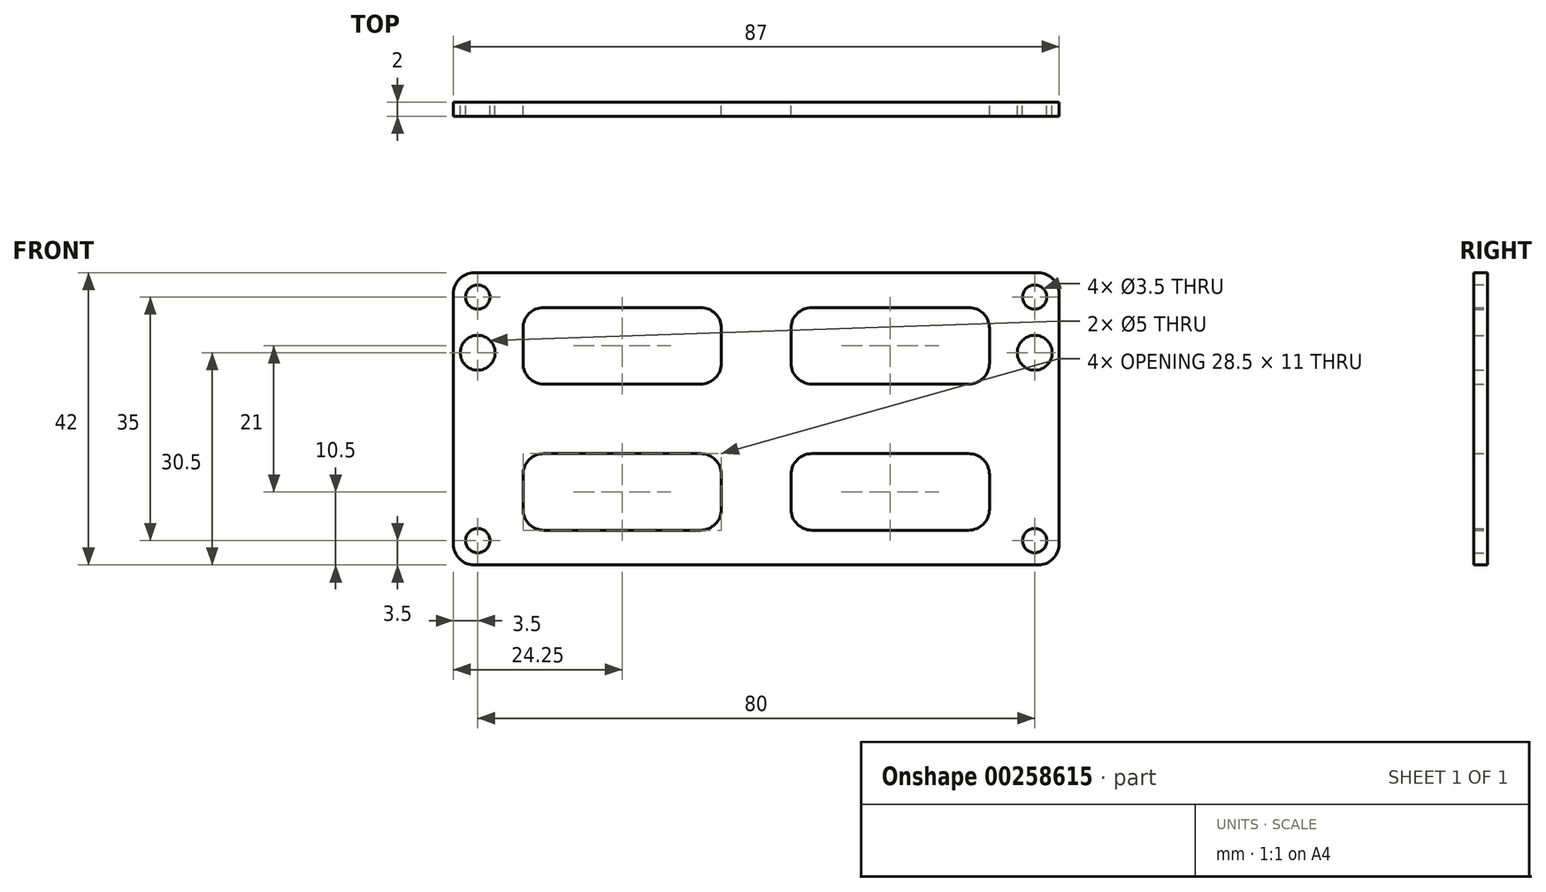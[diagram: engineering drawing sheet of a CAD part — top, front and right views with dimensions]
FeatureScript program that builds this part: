
annotation { "Feature Type Name" : "Feature", "Feature Type Description" : "" }
export const myFeature = defineFeature(function(context is Context, id is Id, definition is map)
    precondition{}
    {
        {
            var Q0;
            Q0=qCreatedBy(makeId("Front.planeOp"),FACE);
            var sketch = newSketch(context, id + "F0", { "sketchPlane" : qUnion([Q0])});
            skLineSegment(sketch, "E0.bottom", {"start": v(40, 17.5) * mm, "end": v(-40, 17.5) * mm, "construction": true});
            skLineSegment(sketch, "E0.top", {"start": v(40, -17.5) * mm, "end": v(-40, -17.5) * mm, "construction": true});
            skLineSegment(sketch, "E0.left", {"start": v(40, 17.5) * mm, "end": v(40, -17.5) * mm, "construction": true});
            skLineSegment(sketch, "E0.right", {"start": v(-40, 17.5) * mm, "end": v(-40, -17.5) * mm, "construction": true});
            skPoint(sketch, "E0.middle", {"position": v(0, 0) * mm});
            skCircle(sketch, "E1", {"center": v(-40, 17.5) * mm, "radius": 1.75 * mm});
            skCircle(sketch, "E2", {"center": v(-40, -17.5) * mm, "radius": 1.75 * mm});
            skCircle(sketch, "E3", {"center": v(40, -17.5) * mm, "radius": 1.75 * mm});
            skCircle(sketch, "E4", {"center": v(40, 17.5) * mm, "radius": 1.75 * mm});
            skLineSegment(sketch, "E5.bottom", {"start": v(-40, 17.5) * mm, "end": v(40, 17.5) * mm, "construction": true});
            skLineSegment(sketch, "E5.top", {"start": v(-40, 9.5) * mm, "end": v(40, 9.5) * mm, "construction": true});
            skLineSegment(sketch, "E5.left", {"start": v(-40, 17.5) * mm, "end": v(-40, 9.5) * mm, "construction": true});
            skLineSegment(sketch, "E5.right", {"start": v(40, 17.5) * mm, "end": v(40, 9.5) * mm, "construction": true});
            skCircle(sketch, "E6", {"center": v(-40, 9.5) * mm, "radius": 2.5 * mm});
            skCircle(sketch, "E7", {"center": v(40, 9.5) * mm, "radius": 2.5 * mm});
            skLineSegment(sketch, "E8.bottom", {"start": v(43.5, 21) * mm, "end": v(-43.5, 21) * mm});
            skLineSegment(sketch, "E8.top", {"start": v(43.5, -21) * mm, "end": v(-43.5, -21) * mm});
            skLineSegment(sketch, "E8.left", {"start": v(43.5, 21) * mm, "end": v(43.5, -21) * mm});
            skLineSegment(sketch, "E8.right", {"start": v(-43.5, 21) * mm, "end": v(-43.5, -21) * mm});
            skLineSegment(sketch, "E9.bottom", {"start": v(5, 5) * mm, "end": v(-5, 5) * mm, "construction": true});
            skLineSegment(sketch, "E9.top", {"start": v(5, -5) * mm, "end": v(-5, -5) * mm, "construction": true});
            skLineSegment(sketch, "E9.left", {"start": v(5, 5) * mm, "end": v(5, -5) * mm, "construction": true});
            skLineSegment(sketch, "E9.right", {"start": v(-5, 5) * mm, "end": v(-5, -5) * mm, "construction": true});
            skLineSegment(sketch, "E10.bottom", {"start": v(-43.5, -21) * mm, "end": v(-33.5, -21) * mm, "construction": true});
            skLineSegment(sketch, "E10.top", {"start": v(-43.5, -16) * mm, "end": v(-33.5, -16) * mm, "construction": true});
            skLineSegment(sketch, "E10.left", {"start": v(-43.5, -21) * mm, "end": v(-43.5, -16) * mm, "construction": true});
            skLineSegment(sketch, "E10.right", {"start": v(-33.5, -21) * mm, "end": v(-33.5, -16) * mm, "construction": true});
            skLineSegment(sketch, "E11.bottom", {"start": v(-43.5, 21) * mm, "end": v(-33.5, 21) * mm, "construction": true});
            skLineSegment(sketch, "E11.top", {"start": v(-43.5, 16) * mm, "end": v(-33.5, 16) * mm, "construction": true});
            skLineSegment(sketch, "E11.left", {"start": v(-43.5, 21) * mm, "end": v(-43.5, 16) * mm, "construction": true});
            skLineSegment(sketch, "E11.right", {"start": v(-33.5, 21) * mm, "end": v(-33.5, 16) * mm, "construction": true});
            skLineSegment(sketch, "E12.bottom", {"start": v(43.5, 21) * mm, "end": v(33.5, 21) * mm, "construction": true});
            skLineSegment(sketch, "E12.top", {"start": v(43.5, 16) * mm, "end": v(33.5, 16) * mm, "construction": true});
            skLineSegment(sketch, "E12.left", {"start": v(43.5, 21) * mm, "end": v(43.5, 16) * mm, "construction": true});
            skLineSegment(sketch, "E12.right", {"start": v(33.5, 21) * mm, "end": v(33.5, 16) * mm, "construction": true});
            skLineSegment(sketch, "E13.bottom", {"start": v(43.5, -21) * mm, "end": v(33.5, -21) * mm, "construction": true});
            skLineSegment(sketch, "E13.top", {"start": v(43.5, -16) * mm, "end": v(33.5, -16) * mm, "construction": true});
            skLineSegment(sketch, "E13.left", {"start": v(43.5, -21) * mm, "end": v(43.5, -16) * mm, "construction": true});
            skLineSegment(sketch, "E13.right", {"start": v(33.5, -21) * mm, "end": v(33.5, -16) * mm, "construction": true});
            skLineSegment(sketch, "E14.bottom", {"start": v(-5, 5) * mm, "end": v(-33.5, 5) * mm});
            skLineSegment(sketch, "E14.top", {"start": v(-5, 16) * mm, "end": v(-33.5, 16) * mm});
            skLineSegment(sketch, "E14.left", {"start": v(-5, 5) * mm, "end": v(-5, 16) * mm});
            skLineSegment(sketch, "E14.right", {"start": v(-33.5, 5) * mm, "end": v(-33.5, 16) * mm});
            skLineSegment(sketch, "E15.bottom", {"start": v(-5, -5) * mm, "end": v(-33.5, -5) * mm});
            skLineSegment(sketch, "E15.top", {"start": v(-5, -16) * mm, "end": v(-33.5, -16) * mm});
            skLineSegment(sketch, "E15.left", {"start": v(-5, -5) * mm, "end": v(-5, -16) * mm});
            skLineSegment(sketch, "E15.right", {"start": v(-33.5, -5) * mm, "end": v(-33.5, -16) * mm});
            skLineSegment(sketch, "E16.bottom", {"start": v(5, -5) * mm, "end": v(33.5, -5) * mm});
            skLineSegment(sketch, "E16.top", {"start": v(5, -16) * mm, "end": v(33.5, -16) * mm});
            skLineSegment(sketch, "E16.left", {"start": v(5, -5) * mm, "end": v(5, -16) * mm});
            skLineSegment(sketch, "E16.right", {"start": v(33.5, -5) * mm, "end": v(33.5, -16) * mm});
            skLineSegment(sketch, "E17.bottom", {"start": v(5, 5) * mm, "end": v(33.5, 5) * mm});
            skLineSegment(sketch, "E17.top", {"start": v(5, 16) * mm, "end": v(33.5, 16) * mm});
            skLineSegment(sketch, "E17.left", {"start": v(5, 5) * mm, "end": v(5, 16) * mm});
            skLineSegment(sketch, "E17.right", {"start": v(33.5, 5) * mm, "end": v(33.5, 16) * mm});
            skSolve(sketch);
        }
        {
            var Q0;
            Q0=makeQuery(id+"F0.imprint","IMPRINT",FACE,{"disambiguationData":[TD([[makeQuery(id+"F0.imprint","IMPRINT",EDGE,{"derivedFrom":sQuery(id+"F0.wireOp",EDGE,"E1")}),-1.0]])]});
            extrude(context, id + "F1", {"entities" : qUnion([Q0]), "depth" : 2 * mm});
        }
        {
            var Q0;
            Q0=makeQuery(id+"F1.opExtrude","SWEPT_EDGE",EDGE,{"disambiguationData":[OSD([sQuery(id+"F0.wireOp",EDGE,"E8.bottom"),sQuery(id+"F0.wireOp",EDGE,"E8.right")])]});
            var Q1;
            Q1=makeQuery(id+"F1.opExtrude","SWEPT_EDGE",EDGE,{"disambiguationData":[OSD([sQuery(id+"F0.wireOp",EDGE,"E8.top"),sQuery(id+"F0.wireOp",EDGE,"E8.right")])]});
            var Q2;
            Q2=makeQuery(id+"F1.opExtrude","SWEPT_EDGE",EDGE,{"disambiguationData":[OSD([sQuery(id+"F0.wireOp",EDGE,"E8.top"),sQuery(id+"F0.wireOp",EDGE,"E8.left")])]});
            var Q3;
            Q3=makeQuery(id+"F1.opExtrude","SWEPT_EDGE",EDGE,{"disambiguationData":[OSD([sQuery(id+"F0.wireOp",EDGE,"E8.bottom"),sQuery(id+"F0.wireOp",EDGE,"E8.left")])]});
            var Q4;
            Q4=makeQuery(id+"F1.opExtrude","SWEPT_EDGE",EDGE,{"disambiguationData":[OSD([sQuery(id+"F0.wireOp",EDGE,"E14.top"),sQuery(id+"F0.wireOp",EDGE,"E14.left")])]});
            var Q5;
            Q5=makeQuery(id+"F1.opExtrude","SWEPT_EDGE",EDGE,{"disambiguationData":[OSD([sQuery(id+"F0.wireOp",EDGE,"E17.top"),sQuery(id+"F0.wireOp",EDGE,"E17.right")])]});
            var Q6;
            Q6=makeQuery(id+"F1.opExtrude","SWEPT_EDGE",EDGE,{"disambiguationData":[OSD([sQuery(id+"F0.wireOp",EDGE,"E14.top"),sQuery(id+"F0.wireOp",EDGE,"E14.right")])]});
            var Q7;
            Q7=makeQuery(id+"F1.opExtrude","SWEPT_EDGE",EDGE,{"disambiguationData":[OSD([sQuery(id+"F0.wireOp",EDGE,"E15.bottom"),sQuery(id+"F0.wireOp",EDGE,"E15.right")])]});
            var Q8;
            Q8=makeQuery(id+"F1.opExtrude","SWEPT_EDGE",EDGE,{"disambiguationData":[OSD([sQuery(id+"F0.wireOp",EDGE,"E16.bottom"),sQuery(id+"F0.wireOp",EDGE,"E16.left")])]});
            var Q9;
            Q9=makeQuery(id+"F1.opExtrude","SWEPT_EDGE",EDGE,{"disambiguationData":[OSD([sQuery(id+"F0.wireOp",EDGE,"E17.top"),sQuery(id+"F0.wireOp",EDGE,"E17.left")])]});
            var Q10;
            Q10=makeQuery(id+"F1.opExtrude","SWEPT_EDGE",EDGE,{"disambiguationData":[OSD([sQuery(id+"F0.wireOp",EDGE,"E15.top"),sQuery(id+"F0.wireOp",EDGE,"E15.right")])]});
            var Q11;
            Q11=makeQuery(id+"F1.opExtrude","SWEPT_EDGE",EDGE,{"disambiguationData":[OSD([sQuery(id+"F0.wireOp",EDGE,"E14.bottom"),sQuery(id+"F0.wireOp",EDGE,"E14.right")])]});
            var Q12;
            Q12=makeQuery(id+"F1.opExtrude","SWEPT_EDGE",EDGE,{"disambiguationData":[OSD([sQuery(id+"F0.wireOp",EDGE,"E17.bottom"),sQuery(id+"F0.wireOp",EDGE,"E17.left")])]});
            var Q13;
            Q13=makeQuery(id+"F1.opExtrude","SWEPT_EDGE",EDGE,{"disambiguationData":[OSD([sQuery(id+"F0.wireOp",EDGE,"E16.top"),sQuery(id+"F0.wireOp",EDGE,"E16.left")])]});
            var Q14;
            Q14=makeQuery(id+"F1.opExtrude","SWEPT_EDGE",EDGE,{"disambiguationData":[OSD([sQuery(id+"F0.wireOp",EDGE,"E17.bottom"),sQuery(id+"F0.wireOp",EDGE,"E17.right")])]});
            var Q15;
            Q15=makeQuery(id+"F1.opExtrude","SWEPT_EDGE",EDGE,{"disambiguationData":[OSD([sQuery(id+"F0.wireOp",EDGE,"E16.top"),sQuery(id+"F0.wireOp",EDGE,"E16.right")])]});
            var Q16;
            Q16=makeQuery(id+"F1.opExtrude","SWEPT_EDGE",EDGE,{"disambiguationData":[OSD([sQuery(id+"F0.wireOp",EDGE,"E14.bottom"),sQuery(id+"F0.wireOp",EDGE,"E14.left")])]});
            var Q17;
            Q17=makeQuery(id+"F1.opExtrude","SWEPT_EDGE",EDGE,{"disambiguationData":[OSD([sQuery(id+"F0.wireOp",EDGE,"E15.bottom"),sQuery(id+"F0.wireOp",EDGE,"E15.left")])]});
            var Q18;
            Q18=makeQuery(id+"F1.opExtrude","SWEPT_EDGE",EDGE,{"disambiguationData":[OSD([sQuery(id+"F0.wireOp",EDGE,"E15.top"),sQuery(id+"F0.wireOp",EDGE,"E15.left")])]});
            var Q19;
            Q19=makeQuery(id+"F1.opExtrude","SWEPT_EDGE",EDGE,{"disambiguationData":[OSD([sQuery(id+"F0.wireOp",EDGE,"E16.bottom"),sQuery(id+"F0.wireOp",EDGE,"E16.right")])]});
            fillet(context, id + "F2", {"entities" : qUnion([Q0, Q1, Q2, Q3, Q4, Q5, Q6, Q7, Q8, Q9, Q10, Q11, Q12, Q13, Q14, Q15, Q16, Q17, Q18, Q19]), "radius" : 3 * mm, "tangentPropagation" : true, "allowEdgeOverflow" : false});
        }
    });
